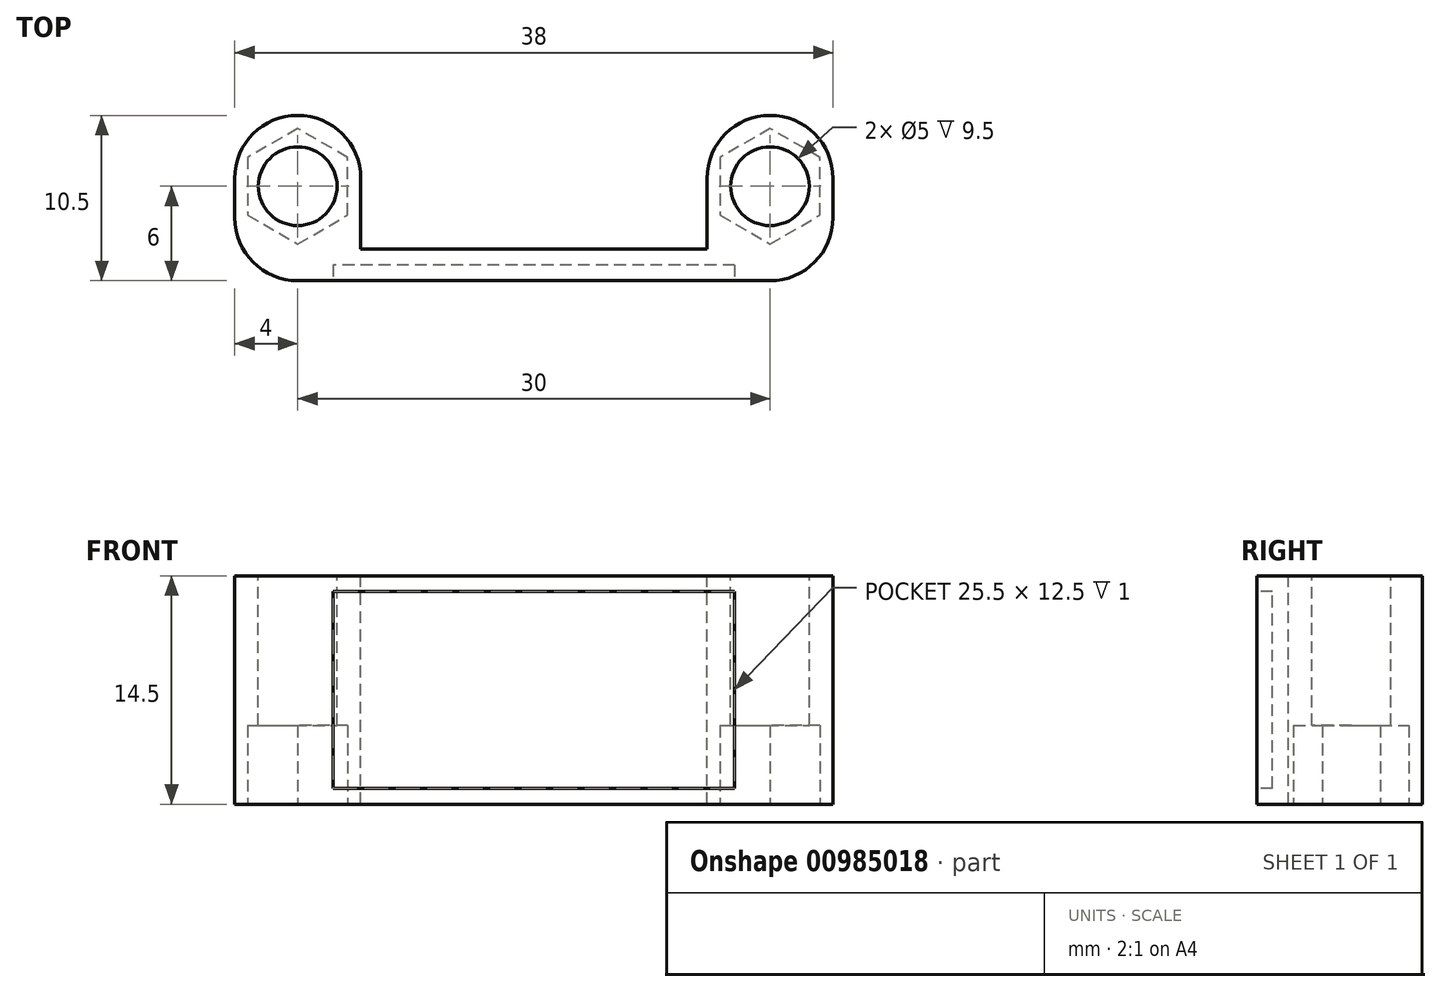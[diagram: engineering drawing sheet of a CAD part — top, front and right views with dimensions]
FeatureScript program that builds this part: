
annotation { "Feature Type Name" : "Feature", "Feature Type Description" : "" }
export const myFeature = defineFeature(function(context is Context, id is Id, definition is map)
    precondition{}
    {
        {
            var Q0;
            Q0=qCreatedBy(makeId("Front.planeOp"),FACE);
            var sketch = newSketch(context, id + "F0", { "sketchPlane" : qUnion([Q0])});
            skLineSegment(sketch, "E0.bottom", {"start": v(19, 7.25) * mm, "end": v(-19, 7.25) * mm});
            skLineSegment(sketch, "E0.top", {"start": v(19, -7.25) * mm, "end": v(-19, -7.25) * mm});
            skLineSegment(sketch, "E0.left", {"start": v(19, 7.25) * mm, "end": v(19, -7.25) * mm});
            skLineSegment(sketch, "E0.right", {"start": v(-19, 7.25) * mm, "end": v(-19, -7.25) * mm});
            skPoint(sketch, "E0.middle", {"position": v(0, 0) * mm});
            skSolve(sketch);
        }
        {
            var Q0;
            Q0=qSketchRegion(id+"F0",true);
            extrude(context, id + "F1", {"entities" : qUnion([Q0]), "depth" : 2 * mm, "offsetDistance" : 25 * mm});
        }
        {
            var Q0;
            Q0=makeQuery(id+"F1.opExtrude","CAP_FACE",FACE,{"disambiguationData":[OSD([sQuery(id+"F0.wireOp",EDGE,"E0.bottom"),sQuery(id+"F0.wireOp",EDGE,"E0.top"),sQuery(id+"F0.wireOp",EDGE,"E0.left"),sQuery(id+"F0.wireOp",EDGE,"E0.right")])],"isStart":false});
            var sketch = newSketch(context, id + "F2", { "sketchPlane" : qUnion([Q0])});
            skLineSegment(sketch, "E1.bottom", {"start": v(12.75, -6.25) * mm, "end": v(-12.75, -6.25) * mm});
            skLineSegment(sketch, "E1.top", {"start": v(12.75, 6.25) * mm, "end": v(-12.75, 6.25) * mm});
            skLineSegment(sketch, "E1.left", {"start": v(12.75, -6.25) * mm, "end": v(12.75, 6.25) * mm});
            skLineSegment(sketch, "E1.right", {"start": v(-12.75, -6.25) * mm, "end": v(-12.75, 6.25) * mm});
            skPoint(sketch, "E1.middle", {"position": v(0, 0) * mm});
            skSolve(sketch);
        }
        {
            var Q0;
            Q0=qSketchRegion(id+"F2",true);
            extrude(context, id + "F3", {"entities" : qUnion([Q0]), "operationType" : NewBodyOperationType.REMOVE, "oppositeDirection" : true, "depth" : 1 * mm, "offsetDistance" : 25 * mm});
        }
        {
            var Q0;
            Q0=makeQuery(id+"F1.opExtrude","CAP_FACE",FACE,{"disambiguationData":[OSD([sQuery(id+"F0.wireOp",EDGE,"E0.bottom"),sQuery(id+"F0.wireOp",EDGE,"E0.top"),sQuery(id+"F0.wireOp",EDGE,"E0.left"),sQuery(id+"F0.wireOp",EDGE,"E0.right")])],"isStart":true});
            var sketch = newSketch(context, id + "F4", { "sketchPlane" : qUnion([Q0])});
            skLineSegment(sketch, "E2.bottom", {"start": v(19, -7.25) * mm, "end": v(11, -7.25) * mm});
            skLineSegment(sketch, "E2.top", {"start": v(19, 7.25) * mm, "end": v(11, 7.25) * mm});
            skLineSegment(sketch, "E2.left", {"start": v(19, -7.25) * mm, "end": v(19, 7.25) * mm});
            skLineSegment(sketch, "E2.right", {"start": v(11, -7.25) * mm, "end": v(11, 7.25) * mm});
            skLineSegment(sketch, "E3.bottom", {"start": v(-19, -7.25) * mm, "end": v(-11, -7.25) * mm});
            skLineSegment(sketch, "E3.top", {"start": v(-19, 7.25) * mm, "end": v(-11, 7.25) * mm});
            skLineSegment(sketch, "E3.left", {"start": v(-19, -7.25) * mm, "end": v(-19, 7.25) * mm});
            skLineSegment(sketch, "E3.right", {"start": v(-11, -7.25) * mm, "end": v(-11, 7.25) * mm});
            skSolve(sketch);
        }
        {
            var Q0;
            Q0=qSketchRegion(id+"F4",true);
            extrude(context, id + "F5", {"entities" : qUnion([Q0]), "operationType" : NewBodyOperationType.ADD, "depth" : 8.5 * mm, "offsetDistance" : 25 * mm});
        }
        {
            var Q0;
            Q0=makeQuery(id+"F5.boolean.opBoolean","MERGE",FACE,{"derivedFrom":[makeQuery(id+"F1.opExtrude","SWEPT_FACE",FACE,{"disambiguationData":[OSD([sQuery(id+"F0.wireOp",EDGE,"E0.bottom")])]}),makeQuery(id+"F5.opExtrude","SWEPT_FACE",FACE,{"disambiguationData":[OSD([sQuery(id+"F4.wireOp",EDGE,"E2.top")])]}),makeQuery(id+"F5.opExtrude","SWEPT_FACE",FACE,{"disambiguationData":[OSD([sQuery(id+"F4.wireOp",EDGE,"E3.top")])]})]});
            var sketch = newSketch(context, id + "F6", { "sketchPlane" : qUnion([Q0])});
            skCircle(sketch, "E4", {"center": v(-15, 4) * mm, "radius": 2.5 * mm});
            skCircle(sketch, "E5", {"center": v(15, 4) * mm, "radius": 2.5 * mm});
            skSolve(sketch);
        }
        {
            var Q0;
            Q0=qSketchRegion(id+"F6",true);
            extrude(context, id + "F7", {"entities" : qUnion([Q0]), "operationType" : NewBodyOperationType.REMOVE, "oppositeDirection" : true, "depth" : 25 * mm, "offsetDistance" : 25 * mm});
        }
        {
            var Q0;
            Q0=makeQuery(id+"F5.boolean.opBoolean","MERGE",FACE,{"derivedFrom":[makeQuery(id+"F1.opExtrude","SWEPT_FACE",FACE,{"disambiguationData":[OSD([sQuery(id+"F0.wireOp",EDGE,"E0.top")])]}),makeQuery(id+"F5.opExtrude","SWEPT_FACE",FACE,{"disambiguationData":[OSD([sQuery(id+"F4.wireOp",EDGE,"E2.bottom")])]}),makeQuery(id+"F5.opExtrude","SWEPT_FACE",FACE,{"disambiguationData":[OSD([sQuery(id+"F4.wireOp",EDGE,"E3.bottom")])]})]});
            var sketch = newSketch(context, id + "F8", { "sketchPlane" : qUnion([Q0])});
            skCircle(sketch, "E6.cCircle", {"center": v(-15, -4) * mm, "radius": 3.17 * mm, "construction": true});
            skLineSegment(sketch, "E6.0", {"start": v(-11.83, -5.83) * mm, "end": v(-15, -7.67) * mm});
            skLineSegment(sketch, "E6.1", {"start": v(-15, -7.67) * mm, "end": v(-18.18, -5.83) * mm});
            skLineSegment(sketch, "E6.2", {"start": v(-18.18, -5.83) * mm, "end": v(-18.18, -2.17) * mm});
            skLineSegment(sketch, "E6.3", {"start": v(-18.17, -2.17) * mm, "end": v(-15, -0.33) * mm});
            skLineSegment(sketch, "E6.4", {"start": v(-15, -0.33) * mm, "end": v(-11.82, -2.17) * mm});
            skLineSegment(sketch, "E6.5", {"start": v(-11.82, -2.17) * mm, "end": v(-11.82, -5.83) * mm});
            skPoint(sketch, "E6.0.midPoint", {"position": v(-13.41, -6.75) * mm});
            skCircle(sketch, "E7.cCircle", {"center": v(15, -4) * mm, "radius": 3.18 * mm, "construction": true});
            skLineSegment(sketch, "E7.0", {"start": v(18.18, -5.83) * mm, "end": v(15, -7.67) * mm});
            skLineSegment(sketch, "E7.1", {"start": v(15, -7.67) * mm, "end": v(11.82, -5.83) * mm});
            skLineSegment(sketch, "E7.2", {"start": v(11.82, -5.83) * mm, "end": v(11.82, -2.17) * mm});
            skLineSegment(sketch, "E7.3", {"start": v(11.82, -2.17) * mm, "end": v(15, -0.33) * mm});
            skLineSegment(sketch, "E7.4", {"start": v(15, -0.33) * mm, "end": v(18.17, -2.17) * mm});
            skLineSegment(sketch, "E7.5", {"start": v(18.17, -2.17) * mm, "end": v(18.17, -5.83) * mm});
            skPoint(sketch, "E7.0.midPoint", {"position": v(16.59, -6.75) * mm});
            skSolve(sketch);
        }
        {
            var Q0;
            Q0=qSketchRegion(id+"F8",true);
            extrude(context, id + "F9", {"entities" : qUnion([Q0]), "operationType" : NewBodyOperationType.REMOVE, "oppositeDirection" : true, "depth" : 5 * mm, "offsetDistance" : 25 * mm});
        }
        {
            var Q0;
            Q0=makeQuery(id+"F1.opExtrude","CAP_EDGE",EDGE,{"disambiguationData":[OSD([sQuery(id+"F0.wireOp",EDGE,"E0.right")])],"isStart":false});
            var Q1;
            Q1=makeQuery(id+"F5.opExtrude","CAP_EDGE",EDGE,{"disambiguationData":[OSD([sQuery(id+"F4.wireOp",EDGE,"E2.left")])],"isStart":false});
            var Q2;
            Q2=makeQuery(id+"F5.opExtrude","CAP_EDGE",EDGE,{"disambiguationData":[OSD([sQuery(id+"F4.wireOp",EDGE,"E3.right")])],"isStart":false});
            var Q3;
            Q3=makeQuery(id+"F1.opExtrude","CAP_EDGE",EDGE,{"disambiguationData":[OSD([sQuery(id+"F0.wireOp",EDGE,"E0.left")])],"isStart":false});
            var Q4;
            Q4=makeQuery(id+"F5.opExtrude","CAP_EDGE",EDGE,{"disambiguationData":[OSD([sQuery(id+"F4.wireOp",EDGE,"E2.right")])],"isStart":false});
            var Q5;
            Q5=makeQuery(id+"F5.opExtrude","CAP_EDGE",EDGE,{"disambiguationData":[OSD([sQuery(id+"F4.wireOp",EDGE,"E3.left")])],"isStart":false});
            fillet(context, id + "F10", {"entities" : qUnion([Q0, Q1, Q2, Q3, Q4, Q5]), "radius" : 4 * mm, "tangentPropagation" : true, "allowEdgeOverflow" : false});
        }
    });
